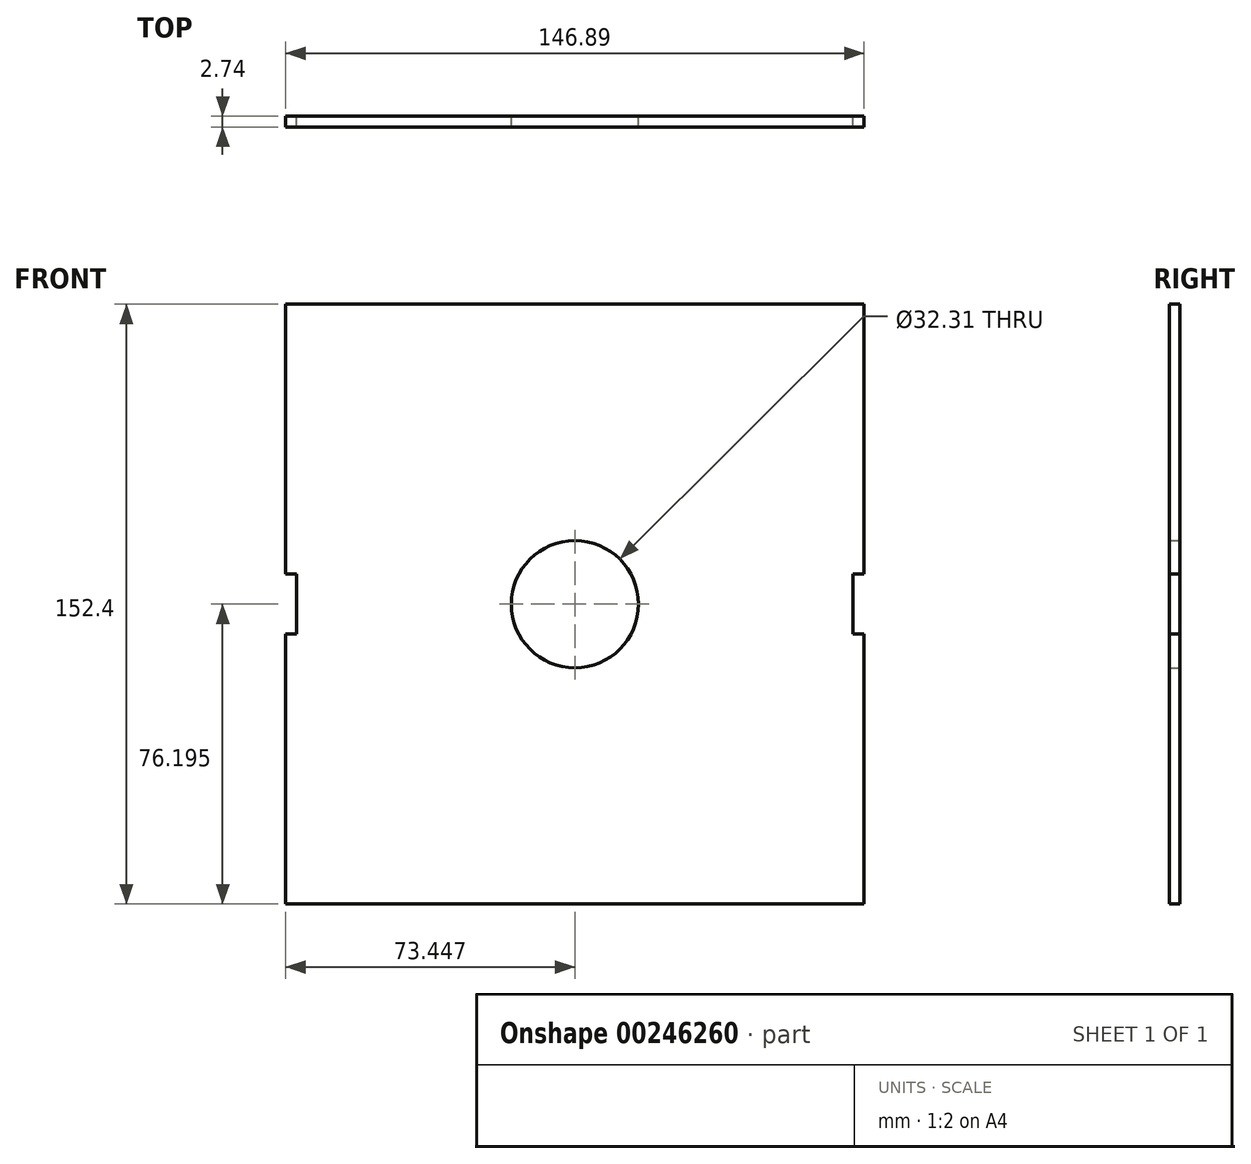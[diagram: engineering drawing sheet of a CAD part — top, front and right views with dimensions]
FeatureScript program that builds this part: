
annotation { "Feature Type Name" : "Feature", "Feature Type Description" : "" }
export const myFeature = defineFeature(function(context is Context, id is Id, definition is map)
    precondition{}
    {
        {
            var Q0;
            Q0=qCreatedBy(makeId("Front.planeOp"),FACE);
            var sketch = newSketch(context, id + "F0", { "sketchPlane" : qUnion([Q0])});
            skLineSegment(sketch, "E0.bottom", {"start": v(-81.08, 118.1) * mm, "end": v(65.81, 118.1) * mm});
            skLineSegment(sketch, "E0.top", {"start": v(-81.08, -34.3) * mm, "end": v(65.81, -34.3) * mm});
            skLineSegment(sketch, "E0.left", {"start": v(-81.08, 118.1) * mm, "end": v(-81.08, -34.3) * mm});
            skLineSegment(sketch, "E0.right", {"start": v(65.81, 118.1) * mm, "end": v(65.81, -34.3) * mm});
            skLineSegment(sketch, "E1", {"start": v(0, 120.84) * mm, "end": v(0, 118.1) * mm});
            skLineSegment(sketch, "E2.MirrorCS", {"start": v(-15.24, 120.84) * mm, "end": v(-15.24, 118.1) * mm});
            skLineSegment(sketch, "E3.MirrorCS", {"start": v(-7.62, -37.05) * mm, "end": v(-15.24, -37.05) * mm});
            skLineSegment(sketch, "E4.MirrorCS", {"start": v(-15.24, -37.05) * mm, "end": v(-15.24, -34.3) * mm});
            skLineSegment(sketch, "E5.MirrorCS", {"start": v(-7.62, -37.05) * mm, "end": v(0, -37.05) * mm});
            skLineSegment(sketch, "E6.MirrorCS", {"start": v(0, -37.05) * mm, "end": v(0, -34.3) * mm});
            skLineSegment(sketch, "E7", {"start": v(-78.33, 49.52) * mm, "end": v(-81.08, 49.52) * mm});
            skLineSegment(sketch, "E8", {"start": v(-15.24, 120.84) * mm, "end": v(0, 120.84) * mm});
            skLineSegment(sketch, "E9.MirrorCS", {"start": v(-78.33, 34.28) * mm, "end": v(-81.08, 34.28) * mm});
            skLineSegment(sketch, "E10", {"start": v(-78.33, 49.52) * mm, "end": v(-78.33, 34.28) * mm});
            skCircle(sketch, "E11", {"center": v(-7.63, 41.9) * mm, "radius": 16.15 * mm});
            skLineSegment(sketch, "E12", {"start": v(-7.63, 118.1) * mm, "end": v(-7.63, -34.3) * mm, "construction": true});
            skLineSegment(sketch, "E13.MirrorCS", {"start": v(63.07, 49.52) * mm, "end": v(65.81, 49.52) * mm});
            skLineSegment(sketch, "E14.MirrorCS", {"start": v(63.07, 49.52) * mm, "end": v(63.07, 34.28) * mm});
            skLineSegment(sketch, "E15.MirrorCS", {"start": v(63.07, 34.28) * mm, "end": v(65.81, 34.28) * mm});
            skSolve(sketch);
        }
        {
            var Q0;
            {var subQ0=sQuery(id+"F0.wireOp",EDGE,"E0.left");Q0=makeQuery(id+"F0.imprint","IMPRINT",FACE,{"disambiguationData":[TD([[makeQuery(id+"F0.imprint","IMPRINT",EDGE,{"derivedFrom":subQ0}),1.0]])]});}
            var Q1;
            Q1=makeQuery(id+"F0.imprint","IMPRINT",FACE,{"disambiguationData":[TD([[makeQuery(id+"F0.imprint","IMPRINT",EDGE,{"derivedFrom":sQuery(id+"F0.wireOp",EDGE,"Afd0L3Ea-njuU-8vJm-DEHg-CMs5uG4HDwlt")}),-1.0]])]});
            extrude(context, id + "F1", {"entities" : qUnion([Q0, Q1]), "depth" : 2.74 * mm});
        }
    });
